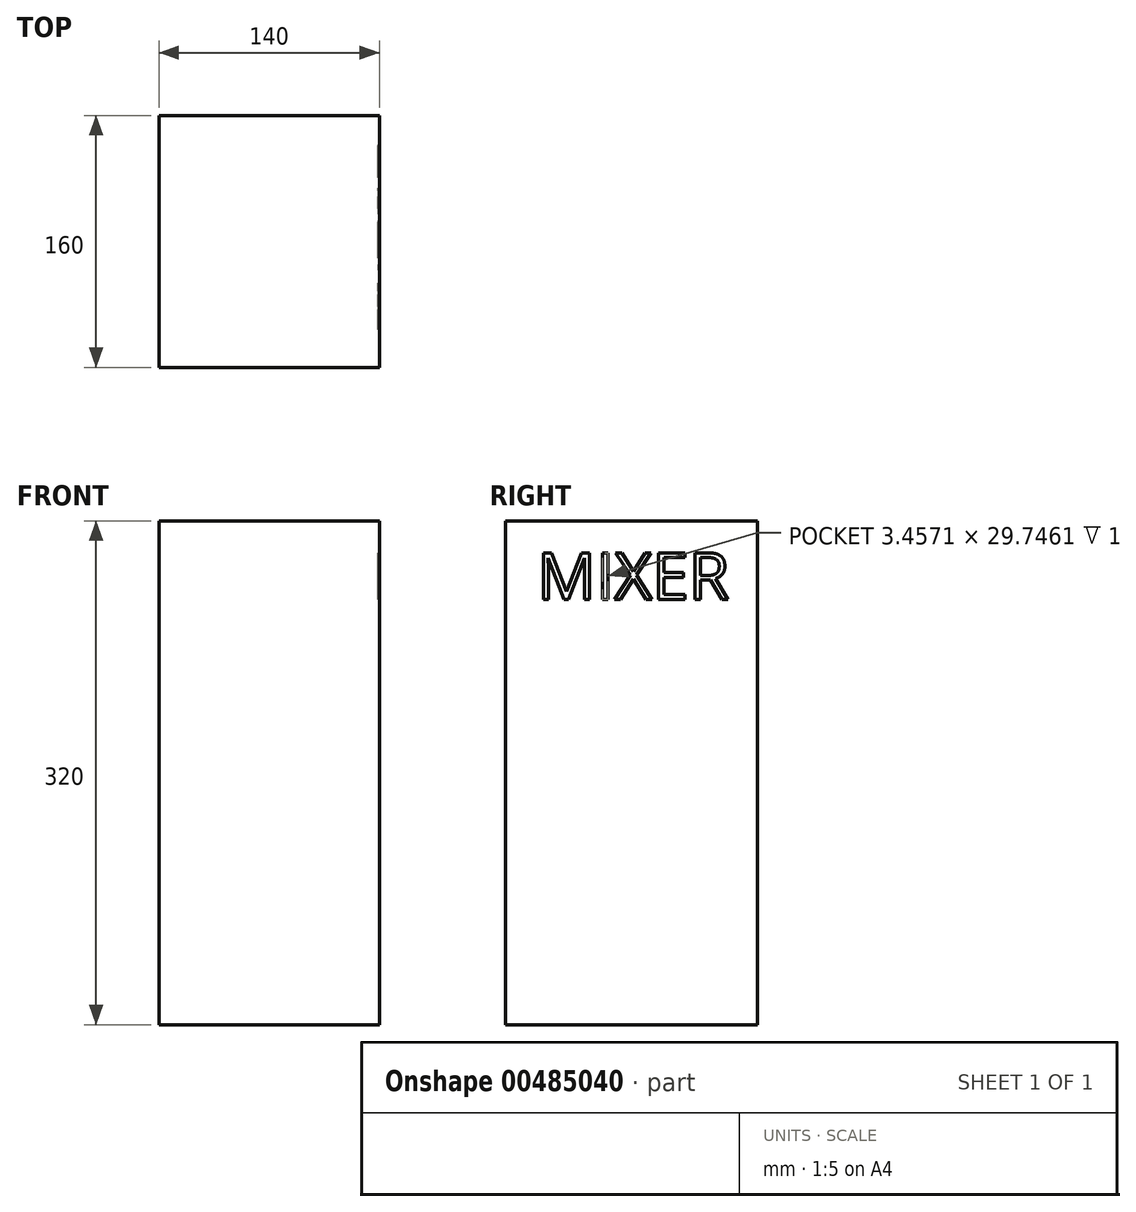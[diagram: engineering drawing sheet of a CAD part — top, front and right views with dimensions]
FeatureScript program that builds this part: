
annotation { "Feature Type Name" : "Feature", "Feature Type Description" : "" }
export const myFeature = defineFeature(function(context is Context, id is Id, definition is map)
    precondition{}
    {
        {
            var Q0;
            Q0=qCreatedBy(makeId("Top.planeOp"),FACE);
            var sketch = newSketch(context, id + "F0", { "sketchPlane" : qUnion([Q0])});
            skLineSegment(sketch, "E0.bottom", {"start": v(70, -80) * mm, "end": v(-70, -80) * mm});
            skLineSegment(sketch, "E0.top", {"start": v(70, 80) * mm, "end": v(-70, 80) * mm});
            skLineSegment(sketch, "E0.left", {"start": v(70, -80) * mm, "end": v(70, 80) * mm});
            skLineSegment(sketch, "E0.right", {"start": v(-70, -80) * mm, "end": v(-70, 80) * mm});
            skPoint(sketch, "E0.middle", {"position": v(0, 0) * mm});
            skSolve(sketch);
        }
        {
            var Q0;
            Q0 = qSketchRegion(id + "F0", true);
            extrude(context, id + "F1", {"entities" : qUnion([Q0]), "depth" : 320 * mm});
        }
        {
            var Q0;
            Q0=makeQuery(id+"F1.opExtrude","SWEPT_FACE",FACE,{"disambiguationData":[OSD([sQuery(id+"F0.wireOp",EDGE,"E0.left")])]});
            var sketch = newSketch(context, id + "F2", { "sketchPlane" : qUnion([Q0])});
            skSolve(sketch);
        }
        {
            var Q0;
            {var subQ0=sQuery(id+"F0.wireOp",EDGE,"E0.left");Q0=makeQuery(id+"F2.imprint","IMPRINT",FACE,{"disambiguationData":[TD([[makeQuery(id+"F2.imprint","IMPRINT",EDGE,{"derivedFrom":makeQuery(id+"F1.opExtrude","CAP_EDGE",EDGE,{"disambiguationData":[OSD([subQ0])],"isStart":true})}),1.0]])]});}
            var sketch = newSketch(context, id + "F3", { "sketchPlane" : qUnion([Q0])});
            skText(sketch, "E1", { "text": "MIXER", "fontName": "OpenSans-Regular.ttf"});
            const initialGuessF3  = {"E1": [-0.06, 0.27, 1, 0, 0.03]};
            skSetInitialGuess(sketch, initialGuessF3);
            skSolve(sketch);
        }
        {
            var Q0;
            Q0 = qSketchRegion(id + "F3", true);
            extrude(context, id + "F4", {"entities" : qUnion([Q0]), "operationType" : NewBodyOperationType.REMOVE, "oppositeDirection" : true, "depth" : 1 * mm});
        }
    });
